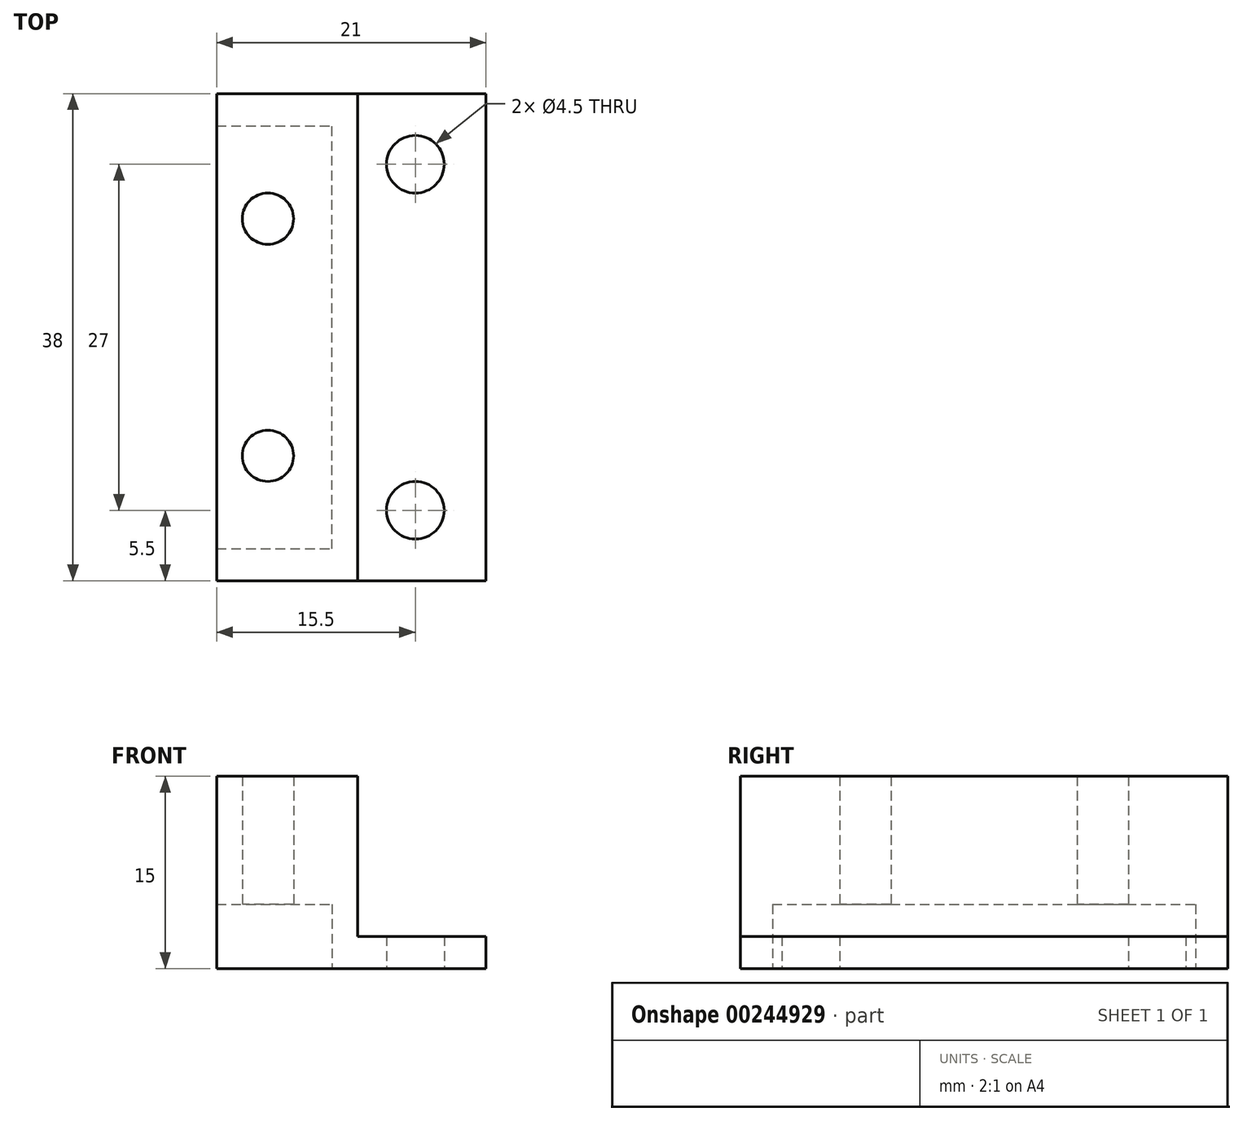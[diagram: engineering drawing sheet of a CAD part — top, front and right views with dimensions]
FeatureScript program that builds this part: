
annotation { "Feature Type Name" : "Feature", "Feature Type Description" : "" }
export const myFeature = defineFeature(function(context is Context, id is Id, definition is map)
    precondition{}
    {
        {
            var Q0;
            Q0=qCreatedBy(makeId("Top.planeOp"),FACE);
            var sketch = newSketch(context, id + "F0", { "sketchPlane" : qUnion([Q0])});
            skLineSegment(sketch, "E0", {"start": v(0, 0) * mm, "end": v(12.5, 0) * mm});
            skLineSegment(sketch, "E1.bottom", {"start": v(12.5, 0) * mm, "end": v(22.5, 0) * mm});
            skLineSegment(sketch, "E1.top", {"start": v(12.5, 38) * mm, "end": v(22.5, 38) * mm});
            skLineSegment(sketch, "E1.left", {"start": v(12.5, 0) * mm, "end": v(12.5, 38) * mm});
            skLineSegment(sketch, "E1.right", {"start": v(22.5, 0) * mm, "end": v(22.5, 38) * mm});
            skLineSegment(sketch, "E2", {"start": v(12.5, 19) * mm, "end": v(17, 19) * mm});
            skPoint(sketch, "E2.endSnap0", {"position": v(12.5, 19) * mm});
            skLineSegment(sketch, "E3", {"start": v(17, 19) * mm, "end": v(17, 32.5) * mm});
            skCircle(sketch, "E4", {"center": v(17, 32.5) * mm, "radius": 2.25 * mm});
            skCircle(sketch, "E5.MirrorC", {"center": v(17, 5.5) * mm, "radius": 2.25 * mm});
            skSolve(sketch);
        }
        {
            var Q0;
            Q0 = qSketchRegion(id + "F0", true);
            extrude(context, id + "F1", {"entities" : qUnion([Q0]), "depth" : 2.5 * mm});
        }
        {
            var Q0;
            Q0=qCreatedBy(makeId("Top.planeOp"),FACE);
            var sketch = newSketch(context, id + "F2", { "sketchPlane" : qUnion([Q0])});
            skLineSegment(sketch, "E6", {"start": v(0, 0) * mm, "end": v(1.5, 0) * mm});
            skLineSegment(sketch, "E7.bottom", {"start": v(1.5, 0) * mm, "end": v(12.5, 0) * mm});
            skLineSegment(sketch, "E7.top", {"start": v(1.5, 38) * mm, "end": v(12.5, 38) * mm});
            skLineSegment(sketch, "E7.left", {"start": v(1.5, 0) * mm, "end": v(1.5, 38) * mm});
            skLineSegment(sketch, "E7.right", {"start": v(12.5, 0) * mm, "end": v(12.5, 38) * mm});
            skLineSegment(sketch, "E8", {"start": v(1.5, 19) * mm, "end": v(5.5, 19) * mm});
            skLineSegment(sketch, "E9", {"start": v(5.5, 19) * mm, "end": v(5.5, 28.25) * mm});
            skCircle(sketch, "E10", {"center": v(5.5, 28.25) * mm, "radius": 2 * mm});
            skCircle(sketch, "E11.MirrorC", {"center": v(5.5, 9.75) * mm, "radius": 2 * mm});
            skSolve(sketch);
        }
        {
            var Q0;
            Q0 = qSketchRegion(id + "F2", true);
            extrude(context, id + "F3", {"entities" : qUnion([Q0]), "operationType" : NewBodyOperationType.ADD, "depth" : 15 * mm});
        }
        {
            var Q0;
            Q0=qCreatedBy(makeId("Top.planeOp"),FACE);
            var sketch = newSketch(context, id + "F4", { "sketchPlane" : qUnion([Q0])});
            skLineSegment(sketch, "E12", {"start": v(0, 0) * mm, "end": v(1.5, 0) * mm});
            skLineSegment(sketch, "E13", {"start": v(1.5, 0) * mm, "end": v(1.5, 2.5) * mm});
            skLineSegment(sketch, "E14.bottom", {"start": v(1.5, 2.5) * mm, "end": v(10.5, 2.5) * mm});
            skLineSegment(sketch, "E14.top", {"start": v(1.5, 35.5) * mm, "end": v(10.5, 35.5) * mm});
            skLineSegment(sketch, "E14.left", {"start": v(1.5, 2.5) * mm, "end": v(1.5, 35.5) * mm});
            skLineSegment(sketch, "E14.right", {"start": v(10.5, 2.5) * mm, "end": v(10.5, 35.5) * mm});
            skSolve(sketch);
        }
        {
            var Q0;
            Q0 = qSketchRegion(id + "F4", true);
            extrude(context, id + "F5", {"entities" : qUnion([Q0]), "operationType" : NewBodyOperationType.REMOVE, "depth" : 5 * mm});
        }
    });
